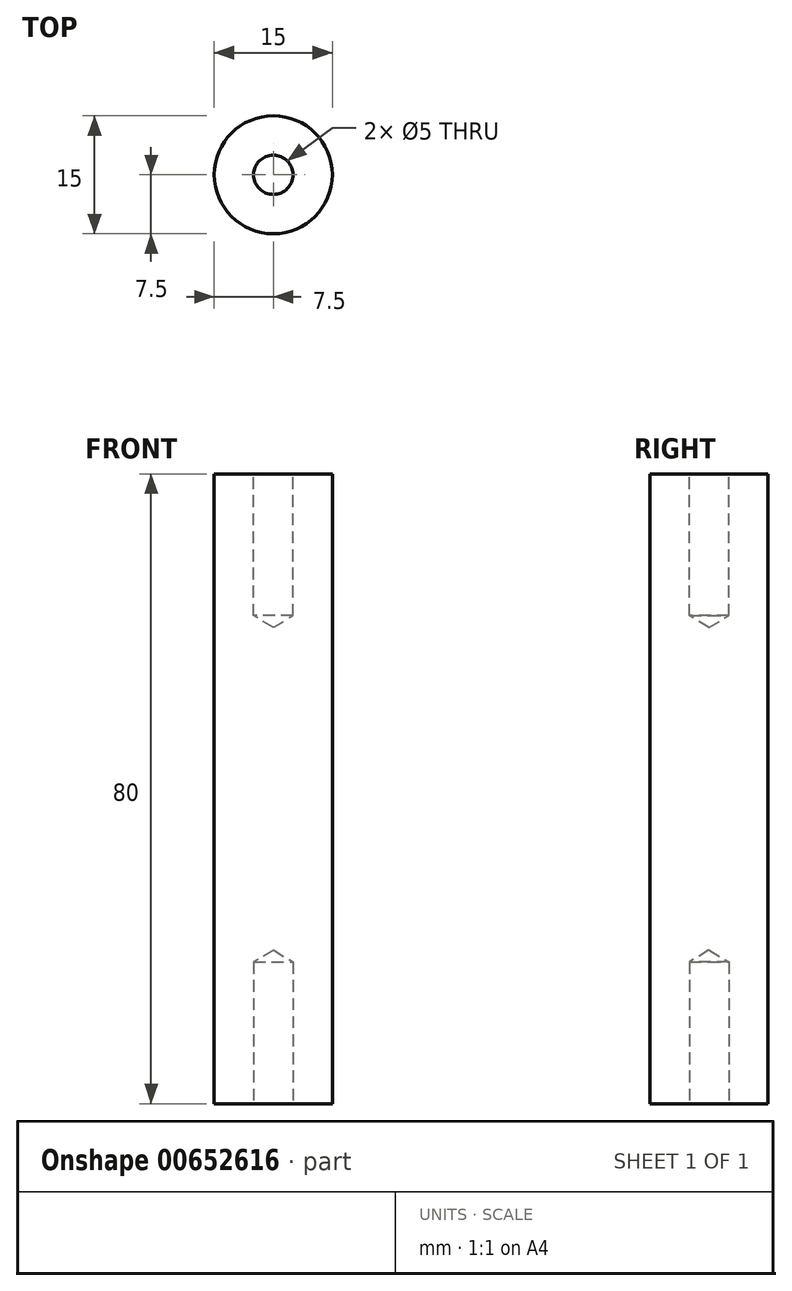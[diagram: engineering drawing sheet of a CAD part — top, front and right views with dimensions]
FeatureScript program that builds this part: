
annotation { "Feature Type Name" : "Feature", "Feature Type Description" : "" }
export const myFeature = defineFeature(function(context is Context, id is Id, definition is map)
    precondition{}
    {
        {
            var Q0;
            Q0=qCreatedBy(makeId("Front.planeOp"),FACE);
            var sketch = newSketch(context, id + "F0", { "sketchPlane" : qUnion([Q0])});
            skLineSegment(sketch, "E0", {"start": v(2, 80) * mm, "end": v(7.5, 80) * mm});
            skLineSegment(sketch, "E1", {"start": v(7.5, 80) * mm, "end": v(7.5, 0) * mm});
            skLineSegment(sketch, "E2", {"start": v(7.5, 0) * mm, "end": v(2, 0) * mm});
            skLineSegment(sketch, "E3", {"start": v(2, 80) * mm, "end": v(2, 65) * mm});
            skLineSegment(sketch, "E4", {"start": v(2, 65) * mm, "end": v(0, 65) * mm});
            skLineSegment(sketch, "E5", {"start": v(2, 0) * mm, "end": v(2, 15) * mm});
            skLineSegment(sketch, "E6", {"start": v(2, 15) * mm, "end": v(0, 15) * mm});
            skPoint(sketch, "E7.orphan", {"position": v(0, 0) * mm});
            skLineSegment(sketch, "E8", {"start": v(0, 0) * mm, "end": v(0, 97.12) * mm, "construction": true});
            skLineSegment(sketch, "E9", {"start": v(0, 65) * mm, "end": v(0, 15) * mm});
            skSolve(sketch);
        }
        {
            var Q0;
            Q0 = qSketchRegion(id + "F0", true);
            var Q1;
            Q1=sQuery(id+"F0.wireOp",EDGE,"E8");
            revolve(context, id + "F1", {"entities" : qUnion([Q0]), "axis" : qUnion([Q1]), "revolveType" : RevolveType.FULL});
        }
        {
            var Q0;
            Q0=makeQuery(id+"F1.opRevolve","SWEPT_FACE",FACE,{"disambiguationData":[OSD([sQuery(id+"F0.wireOp",EDGE,"E0")])]});
            var sketch = newSketch(context, id + "F2", { "sketchPlane" : qUnion([Q0])});
            skCircle(sketch, "E10", {"center": v(0, 0) * mm, "radius": 3 * mm});
            skSolve(sketch);
        }
        {
            var Q0;
            Q0=sQuery(id+"F2.wireOp",VERTEX,"E10.center");
            var Q1;
            Q1=makeQuery(id+"F1.opRevolve","SWEPT_BODY",BODY,{"disambiguationData":[OSD([sQuery(id+"F0.wireOp",EDGE,"E0"),sQuery(id+"F0.wireOp",EDGE,"E1"),sQuery(id+"F0.wireOp",EDGE,"E2"),sQuery(id+"F0.wireOp",EDGE,"E3"),sQuery(id+"F0.wireOp",EDGE,"E4"),sQuery(id+"F0.wireOp",EDGE,"E5"),sQuery(id+"F0.wireOp",EDGE,"E6"),sQuery(id+"F0.wireOp",EDGE,"E9")])]});
            hole(context, id + "F3", {"style" : HoleStyle.SIMPLE, "endStyle" : HoleEndStyle.BLIND, "standardTappedOrClearance" : lookupTablePath({ "standard" : "ISO", "engagement" : "75%", "pitch" : "1 mm", "size" : "M6", "type" : "Tapped" }), "standardBlindInLast" : lookupTablePath({ "standard" : "ISO", "engagement" : "75%", "pitch" : "1 mm", "size" : "M6", "type" : "Tapped" }), "holeDiameter" : 5 * mm, "majorDiameter" : 6 * mm, "showTappedDepth" : true, "holeDepth" : 18 * mm, "isTappedThrough" : true, "tappedDepth" : 15 * mm, "tapClearance" : 3, "locations" : qUnion([Q0]), "scope" : qUnion([Q1])});
        }
        {
            var Q0;
            Q0=makeQuery(id+"F1.opRevolve","SWEPT_FACE",FACE,{"disambiguationData":[OSD([sQuery(id+"F0.wireOp",EDGE,"E2")])]});
            var sketch = newSketch(context, id + "F4", { "sketchPlane" : qUnion([Q0])});
            skCircle(sketch, "E11", {"center": v(0, 0) * mm, "radius": 2.74 * mm});
            skSolve(sketch);
        }
        {
            var Q0;
            Q0=sQuery(id+"F4.wireOp",VERTEX,"E11.center");
            var Q1;
            Q1=makeQuery(id+"F1.opRevolve","SWEPT_BODY",BODY,{"disambiguationData":[OSD([sQuery(id+"F0.wireOp",EDGE,"E0"),sQuery(id+"F0.wireOp",EDGE,"E1"),sQuery(id+"F0.wireOp",EDGE,"E2"),sQuery(id+"F0.wireOp",EDGE,"E3"),sQuery(id+"F0.wireOp",EDGE,"E4"),sQuery(id+"F0.wireOp",EDGE,"E5"),sQuery(id+"F0.wireOp",EDGE,"E6"),sQuery(id+"F0.wireOp",EDGE,"E9")])]});
            hole(context, id + "F5", {"style" : HoleStyle.SIMPLE, "endStyle" : HoleEndStyle.BLIND, "standardTappedOrClearance" : lookupTablePath({ "standard" : "ISO", "engagement" : "75%", "pitch" : "1 mm", "size" : "M6", "type" : "Tapped" }), "standardBlindInLast" : lookupTablePath({ "standard" : "ISO", "engagement" : "75%", "pitch" : "1 mm", "size" : "M6", "type" : "Tapped" }), "holeDiameter" : 5 * mm, "majorDiameter" : 6 * mm, "showTappedDepth" : true, "holeDepth" : 18 * mm, "isTappedThrough" : true, "tappedDepth" : 15 * mm, "tapClearance" : 3, "locations" : qUnion([Q0]), "scope" : qUnion([Q1])});
        }
    });
